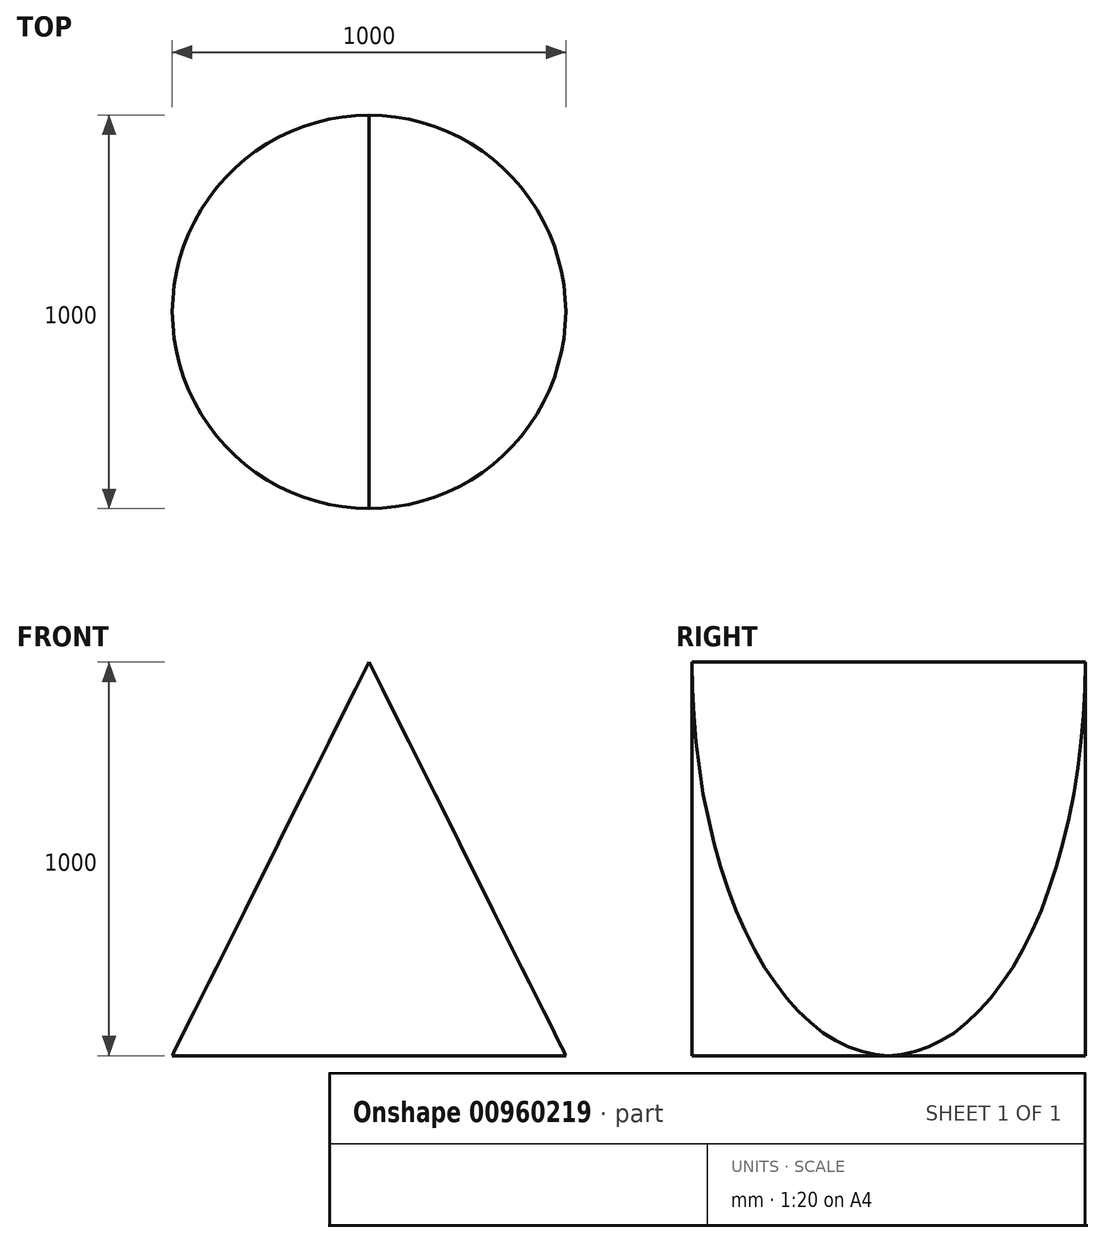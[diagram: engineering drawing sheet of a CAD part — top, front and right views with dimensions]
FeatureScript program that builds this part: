
annotation { "Feature Type Name" : "Feature", "Feature Type Description" : "" }
export const myFeature = defineFeature(function(context is Context, id is Id, definition is map)
    precondition{}
    {
        {
            var Q0;
            Q0=qCreatedBy(makeId("Top.planeOp"),FACE);
            var sketch = newSketch(context, id + "F0", { "sketchPlane" : qUnion([Q0])});
            skCircle(sketch, "E0", {"center": v(0, 0) * mm, "radius": 500 * mm});
            skSolve(sketch);
        }
        {
            var Q0;
            Q0=qCreatedBy(makeId("Front.planeOp"),FACE);
            var sketch = newSketch(context, id + "F1", { "sketchPlane" : qUnion([Q0])});
            skLineSegment(sketch, "E1", {"start": v(-500, 0) * mm, "end": v(500, 0) * mm});
            skLineSegment(sketch, "E2", {"start": v(500, 0) * mm, "end": v(0, 1000) * mm});
            skLineSegment(sketch, "E3", {"start": v(0, 1000) * mm, "end": v(-500, 0) * mm});
            skSolve(sketch);
        }
        {
            var Q0;
            Q0=qCreatedBy(makeId("Right.planeOp"),FACE);
            var sketch = newSketch(context, id + "F2", { "sketchPlane" : qUnion([Q0])});
            skLineSegment(sketch, "E4.bottom", {"start": v(-500, 0) * mm, "end": v(500, 0) * mm});
            skLineSegment(sketch, "E4.top", {"start": v(-500, 1000) * mm, "end": v(500, 1000) * mm});
            skLineSegment(sketch, "E4.left", {"start": v(-500, 0) * mm, "end": v(-500, 1000) * mm});
            skLineSegment(sketch, "E4.right", {"start": v(500, 0) * mm, "end": v(500, 1000) * mm});
            skPoint(sketch, "E5.0", {"position": v(0, 1000) * mm});
            skSolve(sketch);
        }
        {
            var Q0;
            Q0=makeQuery(id+"F0.imprint","IMPRINT",FACE,{"disambiguationData":[TD([[makeQuery(id+"F0.imprint","IMPRINT",EDGE,{"derivedFrom":sQuery(id+"F0.wireOp",EDGE,"E0")}),1.0]])]});
            var Q1;
            Q1=sQuery(id+"F2.wireOp",VERTEX,"E5.0");
            extrude(context, id + "F3", {"entities" : qUnion([Q0]), "endBound" : BoundingType.UP_TO_VERTEX, "depth" : 25.4 * mm, "endBoundEntityVertex" : qUnion([Q1]), "offsetDistance" : 25.4 * mm});
        }
        {
            var Q0;
            Q0=qCreatedBy(makeId("Front.planeOp"),FACE);
            var sketch = newSketch(context, id + "F4", { "sketchPlane" : qUnion([Q0])});
            skLineSegment(sketch, "E6.0", {"start": v(500, 0) * mm, "end": v(0, 1000) * mm});
            skLineSegment(sketch, "E7", {"start": v(500, 0) * mm, "end": v(500, 1000) * mm});
            skLineSegment(sketch, "E8", {"start": v(500, 1000) * mm, "end": v(0, 1000) * mm});
            skSolve(sketch);
        }
        {
            var Q0;
            Q0 = qSketchRegion(id + "F4", true);
            extrude(context, id + "F5", {"entities" : qUnion([Q0]), "endBound" : BoundingType.THROUGH_ALL, "oppositeDirection" : true, "depth" : 25.4 * mm, "offsetDistance" : 25.4 * mm, "hasSecondDirection" : true, "secondDirectionBound" : SecondDirectionBoundingType.THROUGH_ALL, "secondDirectionOppositeDirection" : false, "secondDirectionDepth" : 25.4 * mm});
        }
        {
            var Q0;
            Q0=makeQuery(id+"F5.opExtrude","SWEPT_BODY",BODY,{"disambiguationData":[OSD([sQuery(id+"F4.wireOp",EDGE,"E6.0"),sQuery(id+"F4.wireOp",EDGE,"E7"),sQuery(id+"F4.wireOp",EDGE,"E8")])]});
            var Q1;
            Q1=qCreatedBy(makeId("Right.planeOp"),FACE);
            mirror(context, id + "F6", {"entities" : qUnion([Q0]), "mirrorPlane" : qUnion([Q1])});
        }
        {
            var Q0;
            Q0=makeQuery(id+"F5.opExtrude","SWEPT_BODY",BODY,{"disambiguationData":[OSD([sQuery(id+"F4.wireOp",EDGE,"E6.0"),sQuery(id+"F4.wireOp",EDGE,"E7"),sQuery(id+"F4.wireOp",EDGE,"E8")])]});
            var Q1;
            Q1=makeQuery(id+"F6.opPattern","COPY",BODY,{"derivedFrom":makeQuery(id+"F5.opExtrude","SWEPT_BODY",BODY,{"disambiguationData":[OSD([sQuery(id+"F4.wireOp",EDGE,"E6.0"),sQuery(id+"F4.wireOp",EDGE,"E7"),sQuery(id+"F4.wireOp",EDGE,"E8")])]}),"instanceName":"1"});
            var Q2;
            Q2=makeQuery(id+"F3.opExtrude","SWEPT_BODY",BODY,{"disambiguationData":[OSD([sQuery(id+"F0.wireOp",EDGE,"E0")])]});
            booleanBodies(context, id + "F7", {"operationType" : BooleanOperationType.SUBTRACTION, "tools" : qUnion([Q0, Q1]), "targets" : qUnion([Q2])});
        }
    });
